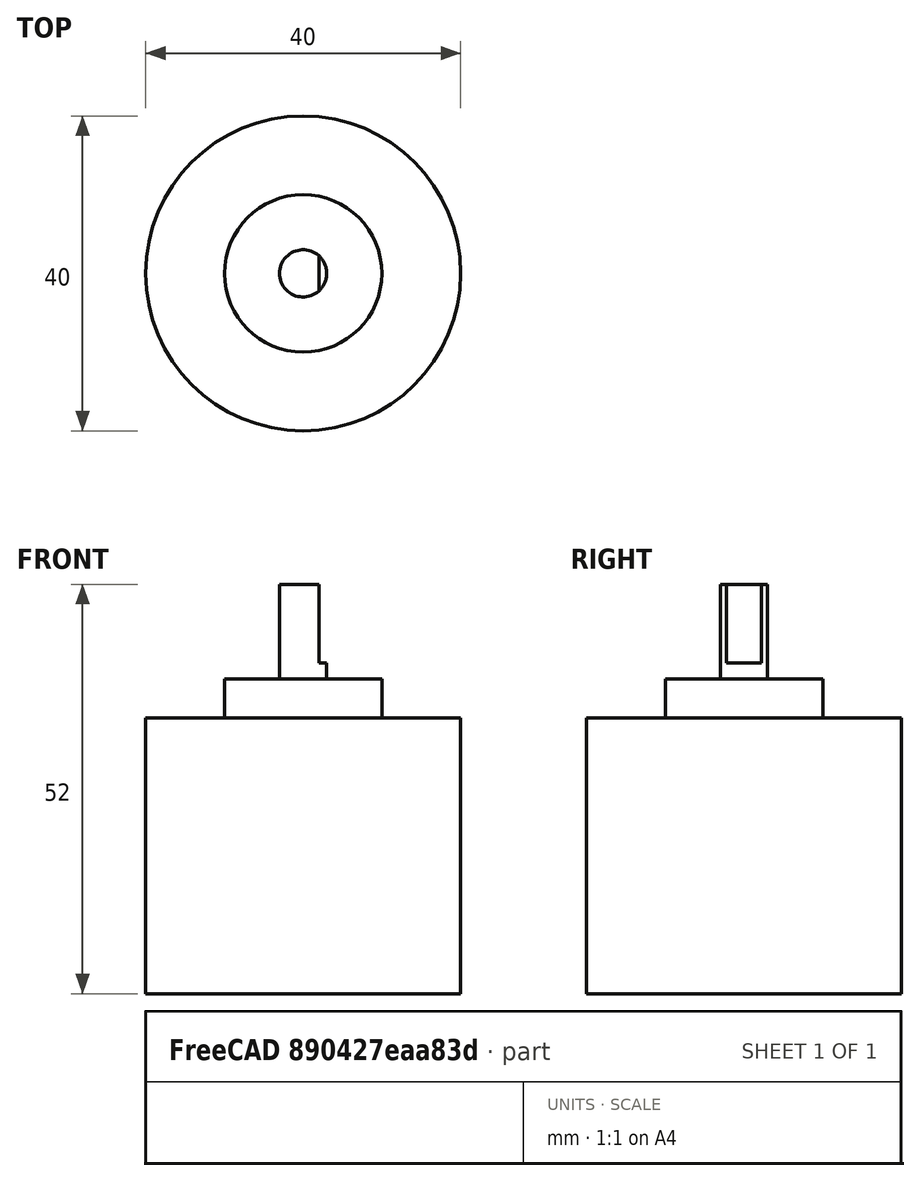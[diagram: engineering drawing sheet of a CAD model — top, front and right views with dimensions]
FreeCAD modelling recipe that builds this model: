
FCSTD DOCUMENT  (FreeCAD 0.18R16110 (Git))
Label: Rotary_Encoder_40mm
License: All rights reserved
LicenseURL: http://en.wikipedia.org/wiki/All_rights_reserved
objects: Part::Cylinder×3, Part::MultiFuse×1, Part::Box×1, Part::Cut×1
note: 6 computed .brp shape members not serialized (recipe doc carries the construction recipe); baked Part::Feature solids carry a one-line shape summary decoded from their .brp

FEATURE [Part::Cylinder] Cylinder
  Angle = 360
  AttacherType = Attacher::AttachEngine3D
  Height = 35
  Placement = pos=(0,0,-35) rot=(0,0,1;0rad)
  Radius = 20
FEATURE [Part::Cylinder] Cylinder001
  Angle = 360
  AttacherType = Attacher::AttachEngine3D
  Height = 5
  Radius = 10
FEATURE [Part::Cylinder] Cylinder002
  Angle = 360
  AttacherType = Attacher::AttachEngine3D
  Height = 12
  Placement = pos=(0,0,5) rot=(0,0,1;0rad)
  Radius = 3
FEATURE [Part::MultiFuse] Fusion  label="Positive Fusion"
  Shapes = -> [Cylinder,Cylinder001,Cylinder002]
FEATURE [Part::Box] Box  label="Cube"
  AttacherType = Attacher::AttachEngine3D
  Height = 10
  Length = 10
  Placement = pos=(2,-5,7) rot=(0,0,1;0rad)
  Width = 10
FEATURE [Part::Cut] Cut
  Base = -> Fusion
  Tool = -> Box
